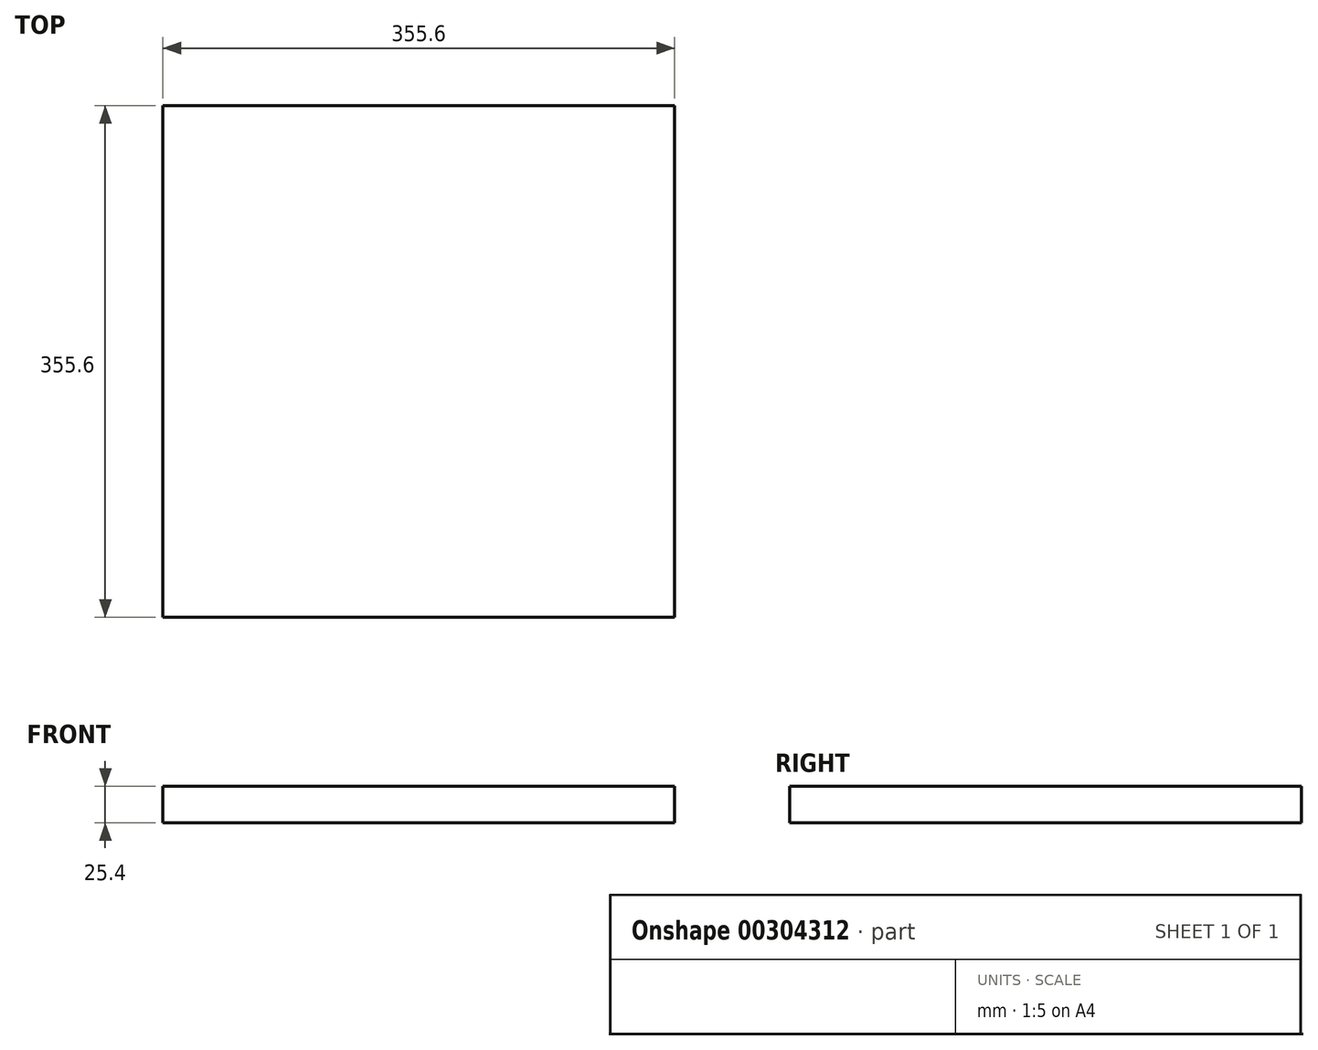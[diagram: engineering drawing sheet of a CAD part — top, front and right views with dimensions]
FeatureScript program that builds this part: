
annotation { "Feature Type Name" : "Feature", "Feature Type Description" : "" }
export const myFeature = defineFeature(function(context is Context, id is Id, definition is map)
    precondition{}
    {
        {
            var Q0;
            Q0=qCreatedBy(makeId("Top.planeOp"),FACE);
            var sketch = newSketch(context, id + "F0", { "sketchPlane" : qUnion([Q0])});
            skLineSegment(sketch, "E0.bottom", {"start": v(177.8, 177.8) * mm, "end": v(-177.8, 177.8) * mm});
            skLineSegment(sketch, "E0.top", {"start": v(177.8, -177.8) * mm, "end": v(-177.8, -177.8) * mm});
            skLineSegment(sketch, "E0.left", {"start": v(177.8, 177.8) * mm, "end": v(177.8, -177.8) * mm});
            skLineSegment(sketch, "E0.right", {"start": v(-177.8, 177.8) * mm, "end": v(-177.8, -177.8) * mm});
            skPoint(sketch, "E0.middle", {"position": v(0, 0) * mm});
            skSolve(sketch);
        }
        {
            var Q0;
            Q0 = qSketchRegion(id + "F0", true);
            extrude(context, id + "F1", {"entities" : qUnion([Q0]), "depth" : 25.4 * mm});
        }
    });
